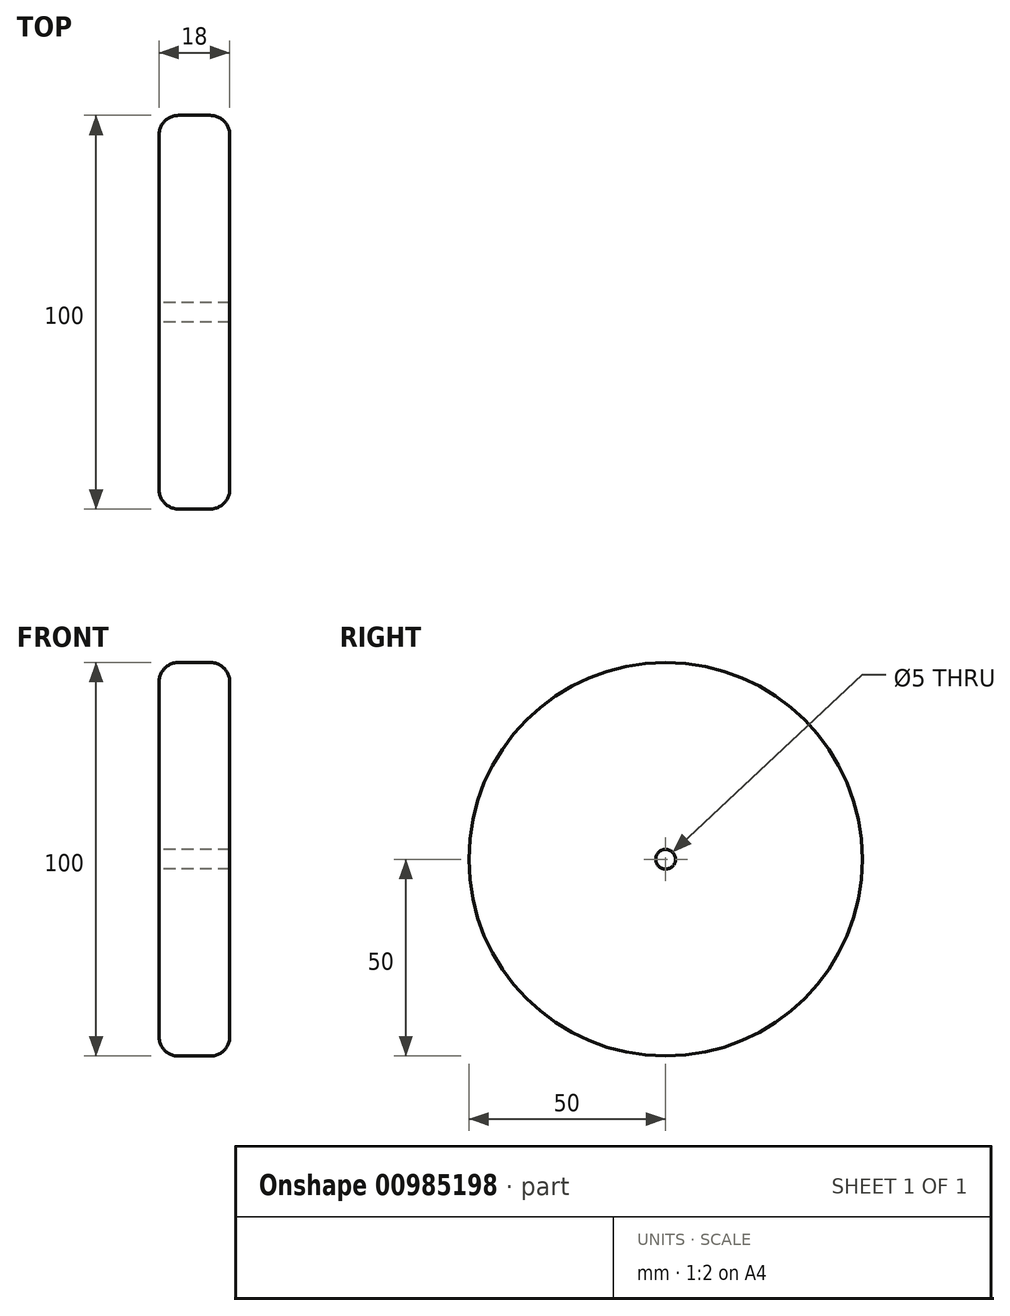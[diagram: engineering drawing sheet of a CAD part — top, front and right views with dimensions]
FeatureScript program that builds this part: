
annotation { "Feature Type Name" : "Feature", "Feature Type Description" : "" }
export const myFeature = defineFeature(function(context is Context, id is Id, definition is map)
    precondition{}
    {
        {
            var Q0;
            Q0=qCreatedBy(makeId("Right.planeOp"),FACE);
            var sketch = newSketch(context, id + "F0", { "sketchPlane" : qUnion([Q0])});
            skCircle(sketch, "E0", {"center": v(0, 0) * mm, "radius": 50 * mm});
            skSolve(sketch);
        }
        {
            var Q0;
            Q0 = qSketchRegion(id + "F0", true);
            extrude(context, id + "F1", {"entities" : qUnion([Q0]), "depth" : 18 * mm, "offsetDistance" : 25 * mm});
        }
        {
            var Q0;
            Q0=makeQuery(id+"F1.opExtrude","CAP_EDGE",EDGE,{"disambiguationData":[OSD([sQuery(id+"F0.wireOp",EDGE,"E0")])],"isStart":false});
            var Q1;
            Q1=makeQuery(id+"F1.opExtrude","CAP_EDGE",EDGE,{"disambiguationData":[OSD([sQuery(id+"F0.wireOp",EDGE,"E0")])],"isStart":true});
            fillet(context, id + "F2", {"entities" : qUnion([Q0, Q1]), "tangentPropagation" : true, "radius" : 5 * mm, "defaultsChanged" : false, "vertexSettings" : [], "allowEdgeOverflow" : false});
        }
        {
            var Q0;
            Q0=sQuery(id+"F0.wireOp",VERTEX,"E0.center");
            var Q1;
            Q1=makeQuery(id+"F1.opExtrude","SWEPT_BODY",BODY,{"disambiguationData":[OSD([sQuery(id+"F0.wireOp",EDGE,"E0")])]});
            hole(context, id + "F3", {"style" : HoleStyle.SIMPLE, "endStyle" : HoleEndStyle.THROUGH, "oppositeDirection" : true, "holeDiameter" : 5 * mm, "majorDiameter" : 5 * mm, "isTappedThrough" : true, "tappedDepth" : 12 * mm, "tapClearance" : 3, "locations" : qUnion([Q0]), "scope" : qUnion([Q1])});
        }
    });
